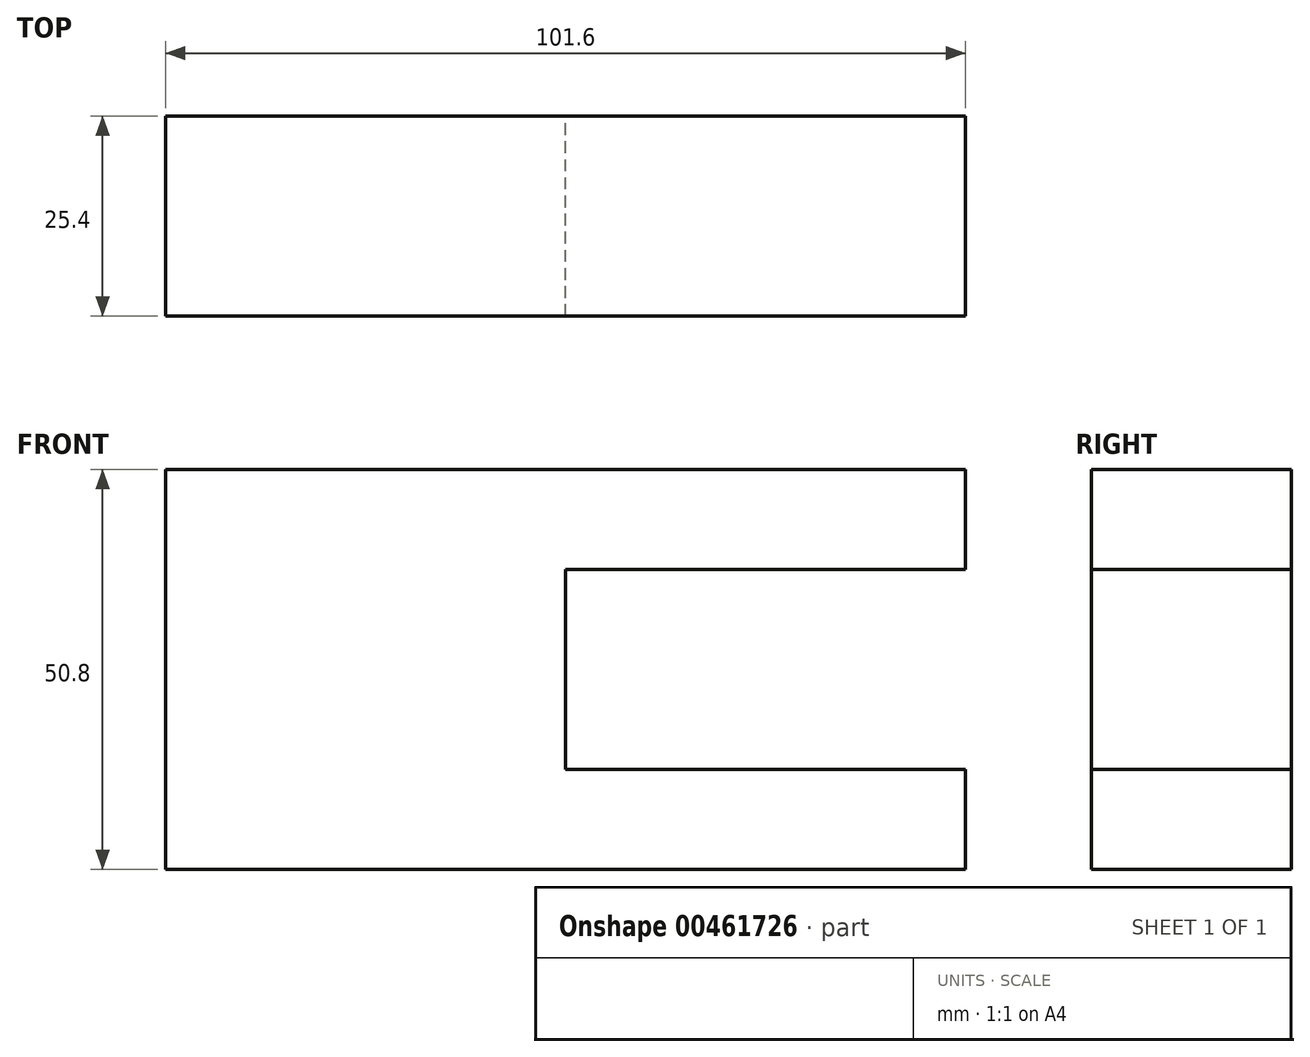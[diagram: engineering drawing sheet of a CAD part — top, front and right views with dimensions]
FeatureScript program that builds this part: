
annotation { "Feature Type Name" : "Feature", "Feature Type Description" : "" }
export const myFeature = defineFeature(function(context is Context, id is Id, definition is map)
    precondition{}
    {
        {
            var Q0;
            Q0=qCreatedBy(makeId("Front.planeOp"),FACE);
            var sketch = newSketch(context, id + "F0", { "sketchPlane" : qUnion([Q0])});
            skLineSegment(sketch, "E0.bottom", {"start": v(-50.8, -25.4) * mm, "end": v(50.8, -25.4) * mm});
            skLineSegment(sketch, "E0.top", {"start": v(-50.8, 25.4) * mm, "end": v(50.8, 25.4) * mm});
            skLineSegment(sketch, "E0.left", {"start": v(-50.8, -25.4) * mm, "end": v(-50.8, 25.4) * mm});
            skLineSegment(sketch, "E0.right", {"start": v(50.8, -25.4) * mm, "end": v(50.8, 25.4) * mm});
            skPoint(sketch, "E0.middle", {"position": v(0, 0) * mm});
            skSolve(sketch);
        }
        {
            var Q0;
            Q0 = qSketchRegion(id + "F0", true);
            extrude(context, id + "F1", {"entities" : qUnion([Q0]), "depth" : 25.4 * mm});
        }
        {
            var Q0;
            Q0=qCreatedBy(makeId("Front.planeOp"),FACE);
            var sketch = newSketch(context, id + "F2", { "sketchPlane" : qUnion([Q0])});
            skLineSegment(sketch, "E1.bottom", {"start": v(50.8, 12.7) * mm, "end": v(0, 12.7) * mm});
            skLineSegment(sketch, "E1.top", {"start": v(50.8, -12.7) * mm, "end": v(0, -12.7) * mm});
            skLineSegment(sketch, "E1.left", {"start": v(50.8, 12.7) * mm, "end": v(50.8, -12.7) * mm});
            skLineSegment(sketch, "E1.right", {"start": v(0, 12.7) * mm, "end": v(0, -12.7) * mm});
            skSolve(sketch);
        }
        {
            var Q0;
            Q0 = qSketchRegion(id + "F2", true);
            extrude(context, id + "F3", {"entities" : qUnion([Q0]), "operationType" : NewBodyOperationType.REMOVE, "endBound" : BoundingType.THROUGH_ALL, "depth" : 25.4 * mm});
        }
    });
